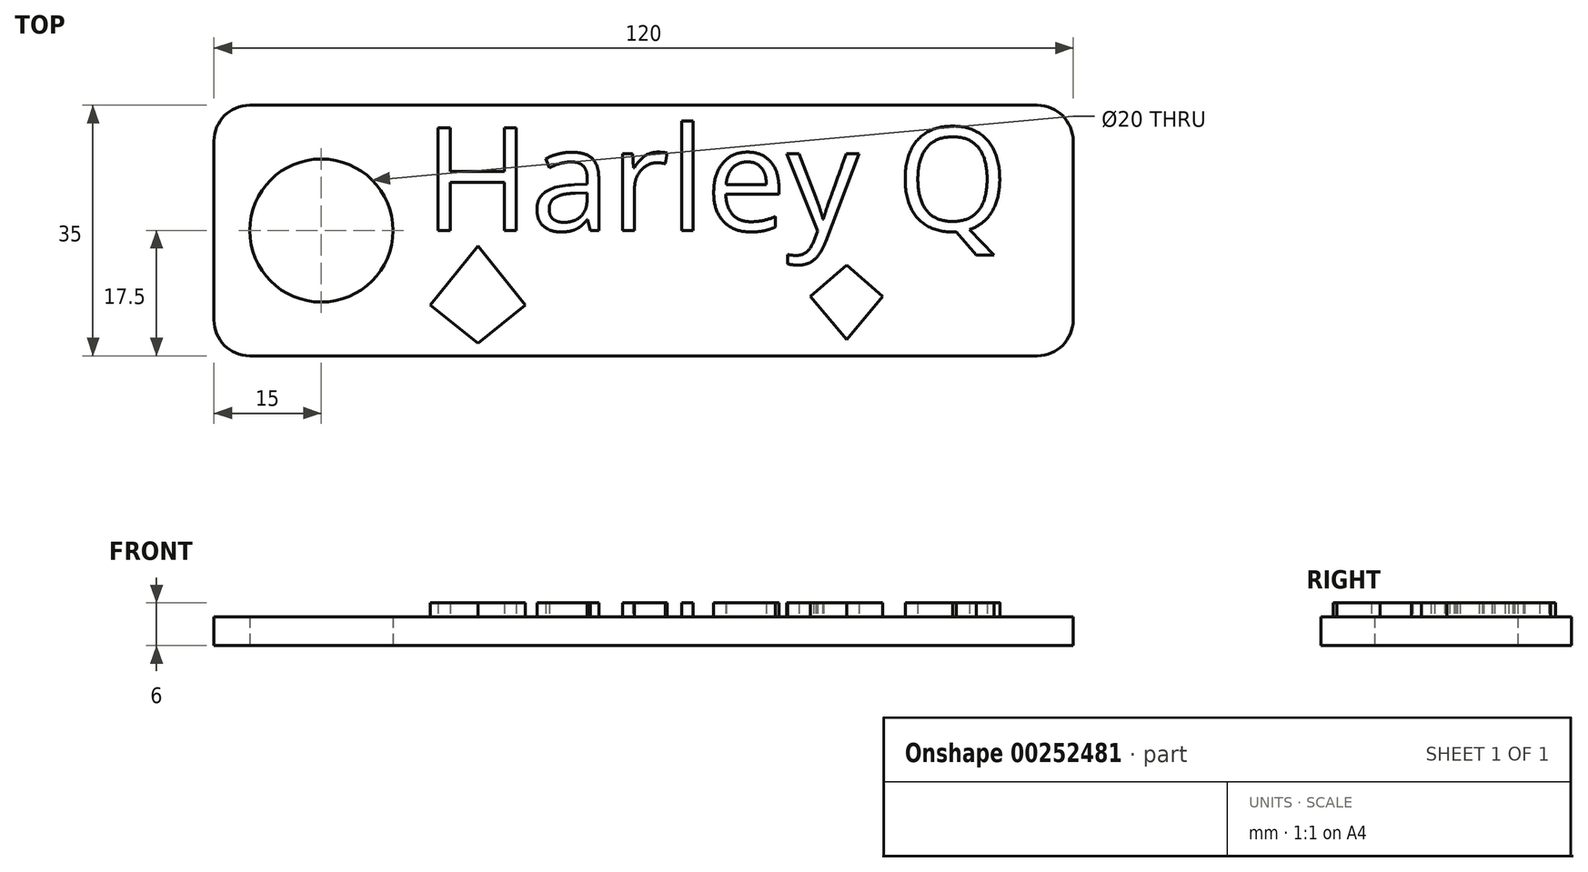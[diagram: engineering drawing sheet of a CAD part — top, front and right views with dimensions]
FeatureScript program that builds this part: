
annotation { "Feature Type Name" : "Feature", "Feature Type Description" : "" }
export const myFeature = defineFeature(function(context is Context, id is Id, definition is map)
    precondition{}
    {
        {
            var Q0;
            Q0=qCreatedBy(makeId("Top.planeOp"),FACE);
            var sketch = newSketch(context, id + "F0", { "sketchPlane" : qUnion([Q0])});
            skLineSegment(sketch, "E0.bottom", {"start": v(-60, 17.5) * mm, "end": v(60, 17.5) * mm});
            skLineSegment(sketch, "E0.top", {"start": v(-60, -17.5) * mm, "end": v(60, -17.5) * mm});
            skLineSegment(sketch, "E0.left", {"start": v(-60, 17.5) * mm, "end": v(-60, -17.5) * mm});
            skLineSegment(sketch, "E0.right", {"start": v(60, 17.5) * mm, "end": v(60, -17.5) * mm});
            skPoint(sketch, "E0.middle", {"position": v(0, 0) * mm});
            skCircle(sketch, "E1", {"center": v(-45, 0) * mm, "radius": 10 * mm});
            skSolve(sketch);
        }
        {
            var Q0;
            Q0=makeQuery(id+"F0.imprint","IMPRINT",FACE,{"disambiguationData":[TD([[makeQuery(id+"F0.imprint","IMPRINT",EDGE,{"derivedFrom":sQuery(id+"F0.wireOp",EDGE,"E0.bottom")}),-1.0]])]});
            extrude(context, id + "F1", {"entities" : qUnion([Q0]), "depth" : 4 * mm});
        }
        {
            var Q0;
            Q0=makeQuery(id+"F1.opExtrude","SWEPT_EDGE",EDGE,{"disambiguationData":[OSD([sQuery(id+"F0.wireOp",EDGE,"E0.bottom"),sQuery(id+"F0.wireOp",EDGE,"E0.right")])]});
            var Q1;
            Q1=makeQuery(id+"F1.opExtrude","SWEPT_EDGE",EDGE,{"disambiguationData":[OSD([sQuery(id+"F0.wireOp",EDGE,"E0.top"),sQuery(id+"F0.wireOp",EDGE,"E0.right")])]});
            var Q2;
            Q2=makeQuery(id+"F1.opExtrude","SWEPT_EDGE",EDGE,{"disambiguationData":[OSD([sQuery(id+"F0.wireOp",EDGE,"E0.top"),sQuery(id+"F0.wireOp",EDGE,"E0.left")])]});
            var Q3;
            Q3=makeQuery(id+"F1.opExtrude","SWEPT_EDGE",EDGE,{"disambiguationData":[OSD([sQuery(id+"F0.wireOp",EDGE,"E0.bottom"),sQuery(id+"F0.wireOp",EDGE,"E0.left")])]});
            fillet(context, id + "F2", {"entities" : qUnion([Q0, Q1, Q2, Q3]), "radius" : 5 * mm, "tangentPropagation" : true, "allowEdgeOverflow" : false});
        }
        {
            var Q0;
            Q0=makeQuery(id+"F1.opExtrude","CAP_FACE",FACE,{"disambiguationData":[OSD([sQuery(id+"F0.wireOp",EDGE,"E0.bottom"),sQuery(id+"F0.wireOp",EDGE,"E0.top"),sQuery(id+"F0.wireOp",EDGE,"E0.left"),sQuery(id+"F0.wireOp",EDGE,"E0.right"),sQuery(id+"F0.wireOp",EDGE,"E1")])],"isStart":false});
            var sketch = newSketch(context, id + "F3", { "sketchPlane" : qUnion([Q0])});
            skText(sketch, "E2", { "text": "Harley Q", "fontName": "OpenSans-Regular.ttf"});
            const initialGuessF3  = {"E2": [-0.03065, 0, 1, 0, 0.01448]};
            skSetInitialGuess(sketch, initialGuessF3);
            skSolve(sketch);
        }
        {
            var Q0;
            Q0=makeQuery(id+"F3.imprint","IMPRINT",FACE,{"disambiguationData":[TD([[makeQuery(id+"F3.imprint","IMPRINT",EDGE,{"derivedFrom":sQuery(id+"F3.wireOp",EDGE,"E2.sketch_text.stroke-0")}),1.0]])]});
            var sketch = newSketch(context, id + "F4", { "sketchPlane" : qUnion([Q0])});
            skLineSegment(sketch, "E3", {"start": v(-23.13, 36.74) * mm, "end": v(-23.13, -37.46) * mm, "construction": true});
            skLineSegment(sketch, "E4", {"start": v(-16.48, -10.44) * mm, "end": v(-23.13, -15.76) * mm});
            skLineSegment(sketch, "E5", {"start": v(-23.13, -2.13) * mm, "end": v(-16.48, -10.44) * mm});
            skLineSegment(sketch, "E6", {"start": v(-23.13, -2.13) * mm, "end": v(-23.13, -2.13) * mm});
            skLineSegment(sketch, "E7.MirrorCS", {"start": v(-23.13, -2.13) * mm, "end": v(-29.78, -10.44) * mm});
            skLineSegment(sketch, "E8.MirrorCS", {"start": v(-29.78, -10.44) * mm, "end": v(-23.13, -15.76) * mm});
            skLineSegment(sketch, "E9", {"start": v(28.35, 37.93) * mm, "end": v(28.35, -47.55) * mm, "construction": true});
            skLineSegment(sketch, "E10", {"start": v(28.35, -4.81) * mm, "end": v(23.3, -9.2) * mm});
            skLineSegment(sketch, "E11", {"start": v(23.3, -9.2) * mm, "end": v(28.35, -15.25) * mm});
            skLineSegment(sketch, "E12.MirrorCS", {"start": v(33.4, -9.2) * mm, "end": v(28.35, -15.25) * mm});
            skLineSegment(sketch, "E13.MirrorCS", {"start": v(28.35, -4.81) * mm, "end": v(33.4, -9.2) * mm});
            skSolve(sketch);
        }
        {
            var Q0;
            Q0 = qSketchRegion(id + "F3", true);
            extrude(context, id + "F5", {"entities" : qUnion([Q0]), "operationType" : NewBodyOperationType.ADD, "depth" : 2 * mm});
        }
        {
            var Q0;
            Q0 = qSketchRegion(id + "F4", true);
            extrude(context, id + "F6", {"entities" : qUnion([Q0]), "operationType" : NewBodyOperationType.ADD, "depth" : 2 * mm});
        }
    });
